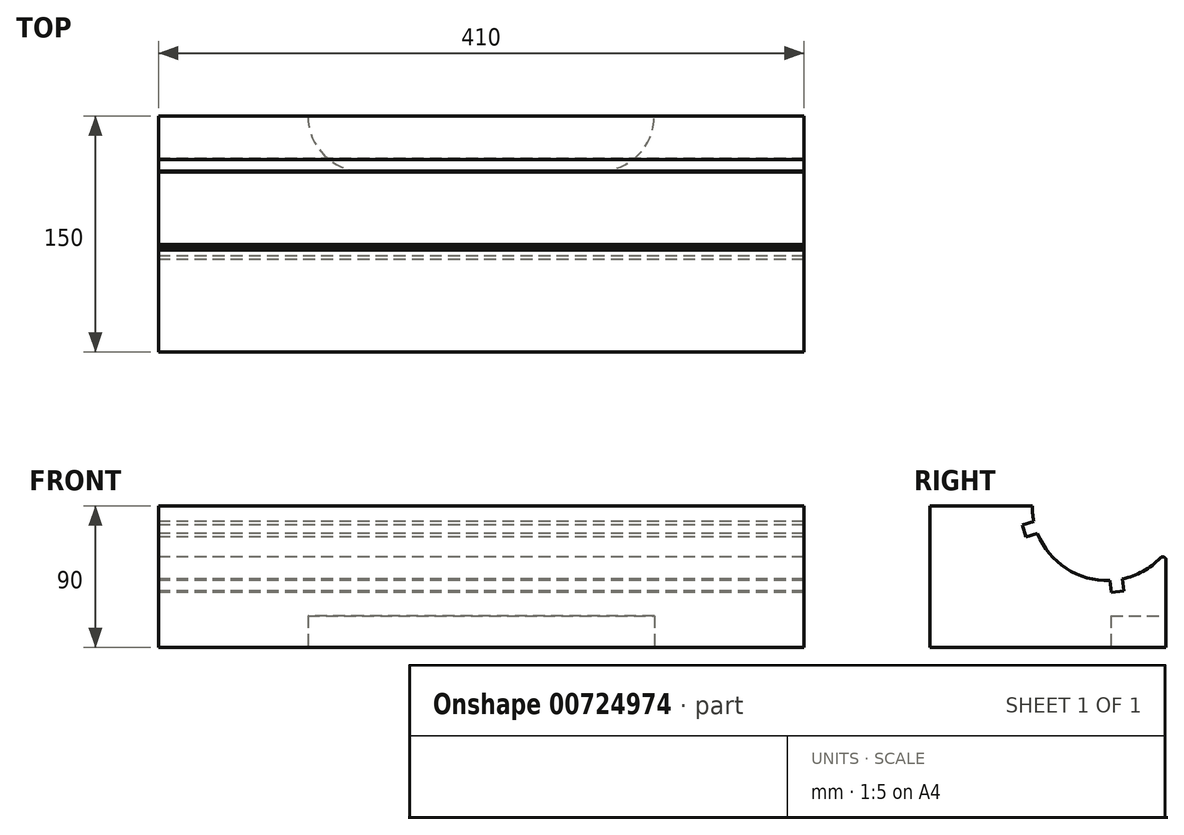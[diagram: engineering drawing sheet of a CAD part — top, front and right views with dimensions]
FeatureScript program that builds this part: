
annotation { "Feature Type Name" : "Feature", "Feature Type Description" : "" }
export const myFeature = defineFeature(function(context is Context, id is Id, definition is map)
    precondition{}
    {
        {
            var Q0;
            Q0=qCreatedBy(makeId("Right.planeOp"),FACE);
            var sketch = newSketch(context, id + "F0", { "sketchPlane" : qUnion([Q0])});
            skLineSegment(sketch, "E0.bottom", {"start": v(0, 0) * mm, "end": v(-150, 0) * mm});
            skLineSegment(sketch, "E0.left", {"start": v(0, 0) * mm, "end": v(0, 60.85) * mm});
            skLineSegment(sketch, "E0.right", {"start": v(-150, 0) * mm, "end": v(-150, 90) * mm});
            skArc(sketch, "E1", {"start": v(-85, 90) * mm, "mid": v(-52.91, 45.07) * mm, "end": v(0, 60.85) * mm});
            skLineSegment(sketch, "E2.trimOffspring", {"start": v(-85, 90) * mm, "end": v(-150, 90) * mm});
            skSolve(sketch);
        }
        {
            var Q0;
            Q0=makeQuery(id+"F0.imprint","IMPRINT",FACE,{"disambiguationData":[TD([[makeQuery(id+"F0.imprint","IMPRINT",EDGE,{"derivedFrom":sQuery(id+"F0.wireOp",EDGE,"E0.bottom")}),-1.0]])]});
            extrude(context, id + "F1", {"entities" : qUnion([Q0]), "depth" : 410 * mm, "offsetDistance" : 25 * mm, "symmetric" : true});
        }
        {
            var Q0;
            Q0=makeQuery(id+"F1.opExtrude","SWEPT_EDGE",EDGE,{"disambiguationData":[OSD([sQuery(id+"F0.wireOp",EDGE,"E0.left"),sQuery(id+"F0.wireOp",EDGE,"E1")])]});
            fillet(context, id + "F2", {"entities" : qUnion([Q0]), "radius" : 2 * mm, "tangentPropagation" : true, "allowEdgeOverflow" : false});
        }
        {
            var Q0;
            Q0=makeQuery(id+"F1.opExtrude","SWEPT_FACE",FACE,{"disambiguationData":[OSD([sQuery(id+"F0.wireOp",EDGE,"E0.bottom")])]});
            var sketch = newSketch(context, id + "F3", { "sketchPlane" : qUnion([Q0])});
            skLineSegment(sketch, "E3", {"start": v(75, 0) * mm, "end": v(-75, 0) * mm, "construction": true});
            skArc(sketch, "E4.0.startCap", {"start": v(75, 35) * mm, "mid": v(110, 0) * mm, "end": v(75, -35) * mm});
            skArc(sketch, "E4.0.endCap", {"start": v(-75, -35) * mm, "mid": v(-110, 0) * mm, "end": v(-75, 35) * mm});
            skLineSegment(sketch, "E4.0.left", {"start": v(75, -35) * mm, "end": v(-75, -35) * mm});
            skLineSegment(sketch, "E4.0.right", {"start": v(75, 35) * mm, "end": v(-75, 35) * mm});
            skSolve(sketch);
        }
        {
            var Q0;
            {var subQ0=sQuery(id+"F3.wireOp",EDGE,"E4.0.right");Q0=makeQuery(id+"F3.imprint","IMPRINT",FACE,{"disambiguationData":[TD([[makeQuery(id+"F3.imprint","IMPRINT",EDGE,{"derivedFrom":subQ0}),1.0]])]});}
            var Q1;
            {var subQ0=sQuery(id+"F3.wireOp",EDGE,"E4.0.left");Q1=makeQuery(id+"F3.imprint","IMPRINT",FACE,{"disambiguationData":[TD([[makeQuery(id+"F3.imprint","IMPRINT",EDGE,{"derivedFrom":subQ0}),-1.0]])]});}
            extrude(context, id + "F4", {"entities" : qUnion([Q0, Q1]), "operationType" : NewBodyOperationType.REMOVE, "oppositeDirection" : true, "depth" : 20 * mm, "offsetDistance" : 25 * mm});
        }
        {
            var Q0;
            Q0=makeQuery(id+"F1.opExtrude","CAP_FACE",FACE,{"disambiguationData":[OSD([sQuery(id+"F0.wireOp",EDGE,"E0.bottom"),sQuery(id+"F0.wireOp",EDGE,"E0.left"),sQuery(id+"F0.wireOp",EDGE,"E0.right"),sQuery(id+"F0.wireOp",EDGE,"E1"),sQuery(id+"F0.wireOp",EDGE,"E2.trimOffspring")])],"isStart":true});
            var sketch = newSketch(context, id + "F5", { "sketchPlane" : qUnion([Q0])});
            skLineSegment(sketch, "E5.0.0", {"start": v(0, 0) * mm, "end": v(0, 55.5) * mm});
            skArc(sketch, "E5.0.1", {"start": v(0, 55.5) * mm, "mid": v(1.25, 57.36) * mm, "end": v(3.43, 56.9) * mm});
            skArc(sketch, "E5.0.2", {"start": v(3.43, 56.9) * mm, "mid": v(55.36, 45.99) * mm, "end": v(85, 90) * mm});
            skLineSegment(sketch, "E5.0.3", {"start": v(85, 90) * mm, "end": v(150, 90) * mm});
            skLineSegment(sketch, "E5.0.4", {"start": v(150, 90) * mm, "end": v(150, 0) * mm});
            skLineSegment(sketch, "E5.0.5", {"start": v(150, 0) * mm, "end": v(0, 0) * mm});
            skArc(sketch, "E6.0", {"start": v(85, 90) * mm, "mid": v(55.36, 45.99) * mm, "end": v(3.43, 56.9) * mm});
            skLineSegment(sketch, "E7", {"start": v(37.5, 90) * mm, "end": v(30.46, 32.7) * mm, "construction": true});
            skLineSegment(sketch, "E8", {"start": v(37.5, 90) * mm, "end": v(102.97, 69.99) * mm, "construction": true});
            skLineSegment(sketch, "E9", {"start": v(78.63, 81.6) * mm, "end": v(91.27, 77.74) * mm});
            skLineSegment(sketch, "E10", {"start": v(91.27, 77.74) * mm, "end": v(88.93, 70.1) * mm});
            skLineSegment(sketch, "E11", {"start": v(88.93, 70.1) * mm, "end": v(76.3, 73.96) * mm});
            skLineSegment(sketch, "E12", {"start": v(76.3, 73.96) * mm, "end": v(78.63, 81.6) * mm});
            skLineSegment(sketch, "E13", {"start": v(28.44, 49) * mm, "end": v(36.38, 48.03) * mm});
            skLineSegment(sketch, "E14", {"start": v(36.38, 48.03) * mm, "end": v(34.77, 34.92) * mm});
            skLineSegment(sketch, "E15", {"start": v(34.77, 34.92) * mm, "end": v(26.83, 35.9) * mm});
            skLineSegment(sketch, "E16", {"start": v(26.83, 35.9) * mm, "end": v(28.44, 49) * mm});
            skSolve(sketch);
        }
        {
            var Q0;
            {var subQ5=sQuery(id+"F5.wireOp",EDGE,"E15");Q0=makeQuery(id+"F5.imprint","IMPRINT",FACE,{"disambiguationData":[TD([[makeQuery(id+"F5.imprint","IMPRINT",EDGE,{"derivedFrom":subQ5}),-1.0]])]});}
            var Q1;
            {var subQ5=sQuery(id+"F5.wireOp",EDGE,"E12");Q1=makeQuery(id+"F5.imprint","IMPRINT",FACE,{"disambiguationData":[TD([[makeQuery(id+"F5.imprint","IMPRINT",EDGE,{"derivedFrom":subQ5}),-1.0]])]});}
            var Q2;
            {var subQ5=sQuery(id+"F5.wireOp",EDGE,"E10");Q2=makeQuery(id+"F5.imprint","IMPRINT",FACE,{"disambiguationData":[TD([[makeQuery(id+"F5.imprint","IMPRINT",EDGE,{"derivedFrom":subQ5}),-1.0]])]});}
            extrude(context, id + "F6", {"entities" : qUnion([Q0, Q1, Q2]), "operationType" : NewBodyOperationType.REMOVE, "endBound" : BoundingType.THROUGH_ALL, "oppositeDirection" : true, "depth" : 25 * mm, "offsetDistance" : 25 * mm});
        }
    });
